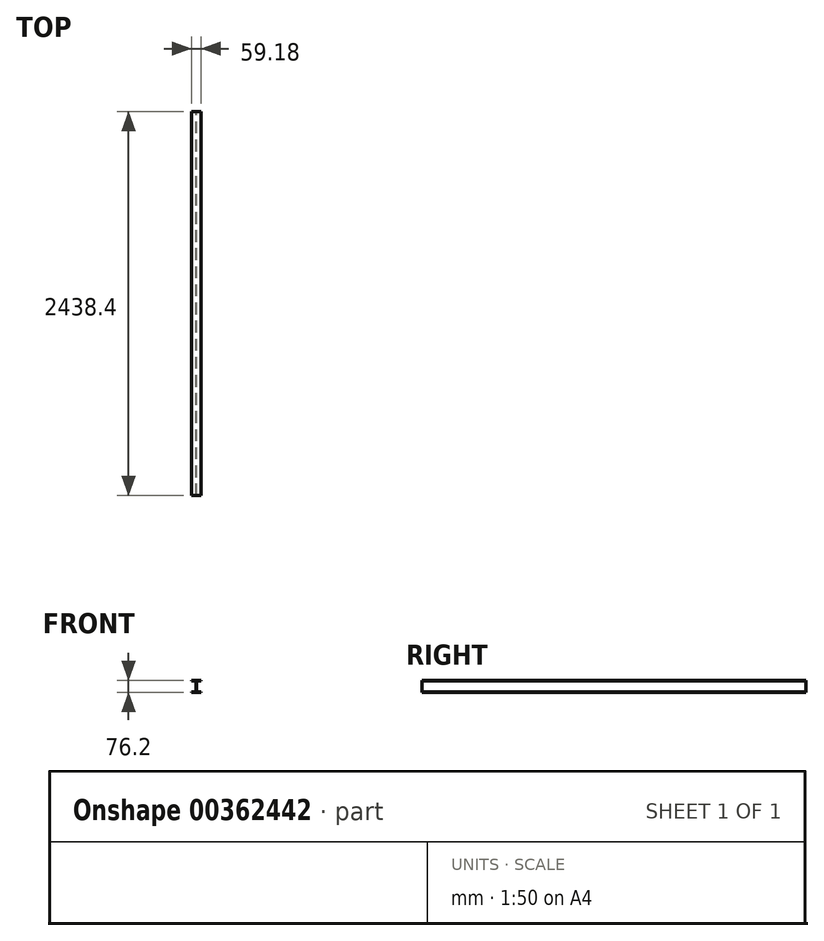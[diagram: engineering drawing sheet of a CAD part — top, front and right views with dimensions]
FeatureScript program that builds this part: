
annotation { "Feature Type Name" : "Feature", "Feature Type Description" : "" }
export const myFeature = defineFeature(function(context is Context, id is Id, definition is map)
    precondition{}
    {
        {
            var Q0;
            Q0=qCreatedBy(makeId("Front.planeOp"),FACE);
            var sketch = newSketch(context, id + "F0", { "sketchPlane" : qUnion([Q0])});
            skLineSegment(sketch, "E0.bottom", {"start": v(0, 0) * mm, "end": v(59.18, 0) * mm});
            skLineSegment(sketch, "E0.top", {"start": v(0, 76.2) * mm, "end": v(59.18, 76.2) * mm});
            skLineSegment(sketch, "E0.left", {"start": v(0, 0) * mm, "end": v(0, 4.32) * mm});
            skLineSegment(sketch, "E0.right", {"start": v(59.18, 0) * mm, "end": v(59.18, 4.32) * mm});
            skLineSegment(sketch, "E1.bottom", {"start": v(0, 71.88) * mm, "end": v(27.43, 71.88) * mm});
            skLineSegment(sketch, "E1.top", {"start": v(0, 4.32) * mm, "end": v(27.43, 4.32) * mm});
            skLineSegment(sketch, "E1.right", {"start": v(27.43, 71.88) * mm, "end": v(27.43, 4.32) * mm});
            skLineSegment(sketch, "E2.bottom", {"start": v(59.18, 71.88) * mm, "end": v(31.75, 71.88) * mm});
            skLineSegment(sketch, "E2.top", {"start": v(59.18, 4.32) * mm, "end": v(31.75, 4.32) * mm});
            skLineSegment(sketch, "E2.right", {"start": v(31.75, 71.88) * mm, "end": v(31.75, 4.32) * mm});
            skLineSegment(sketch, "E3.trimOffspring", {"start": v(59.18, 71.88) * mm, "end": v(59.18, 76.2) * mm});
            skLineSegment(sketch, "E4.trimOffspring", {"start": v(0, 71.88) * mm, "end": v(0, 76.2) * mm});
            skSolve(sketch);
        }
        {
            var Q0;
            Q0 = qSketchRegion(id + "F0", true);
            extrude(context, id + "F1", {"entities" : qUnion([Q0]), "depth" : 2438.4 * mm});
        }
    });
